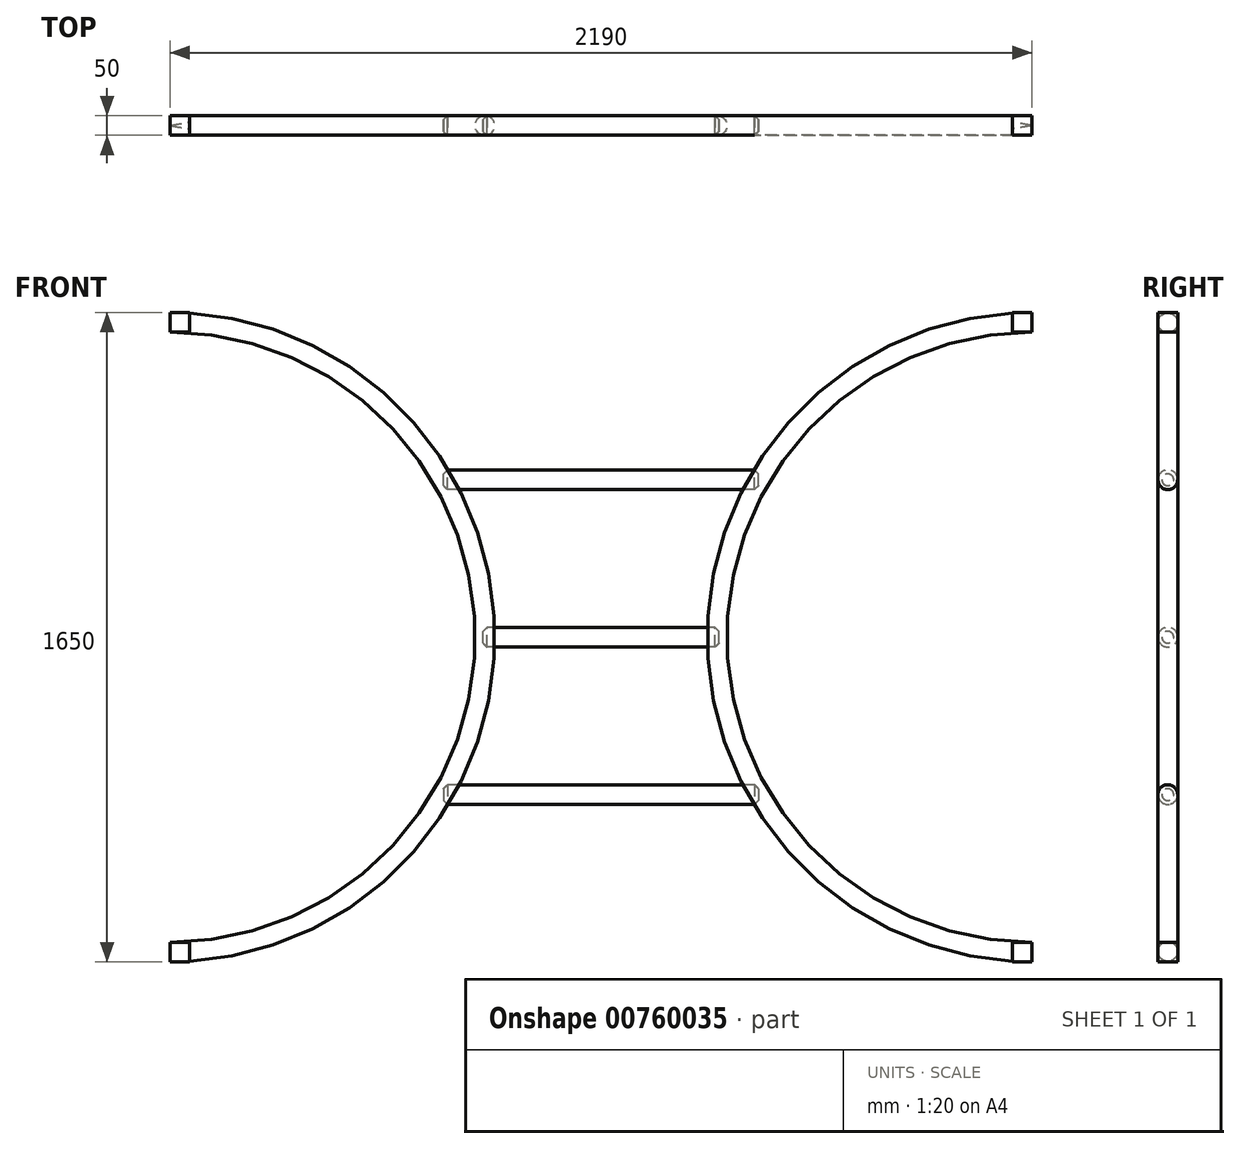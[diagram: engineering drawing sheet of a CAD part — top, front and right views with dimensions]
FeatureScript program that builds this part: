
annotation { "Feature Type Name" : "Feature", "Feature Type Description" : "" }
export const myFeature = defineFeature(function(context is Context, id is Id, definition is map)
    precondition{}
    {
        {
            var Q0;
            Q0=qCreatedBy(makeId("Front.planeOp"),FACE);
            var sketch = newSketch(context, id + "F0", { "sketchPlane" : qUnion([Q0])});
            skArc(sketch, "E0", {"start": v(0, 800) * mm, "mid": v(-800, 0) * mm, "end": v(0, -800) * mm});
            skSolve(sketch);
        }
        {
            var Q0;
            Q0=qCreatedBy(makeId("Right.planeOp"),FACE);
            var sketch = newSketch(context, id + "F1", { "sketchPlane" : qUnion([Q0])});
            skCircle(sketch, "E1", {"center": v(0, 800) * mm, "radius": 25 * mm});
            skSolve(sketch);
        }
        {
            var Q0;
            Q0=makeQuery(id+"F1.imprint","IMPRINT",FACE,{"disambiguationData":[TD([[makeQuery(id+"F1.imprint","IMPRINT",EDGE,{"derivedFrom":sQuery(id+"F1.wireOp",EDGE,"E1")}),1.0]])]});
            var Q1;
            Q1=sQuery(id+"F1.wireOp",EDGE,"E1");
            var Q2;
            Q2=sQuery(id+"F0.wireOp",EDGE,"E0");
            sweep(context, id + "F2", {"profiles" : qUnion([Q0]), "surfaceOperationType" : NewSurfaceOperationType.ADD, "surfaceProfiles" : qUnion([Q1]), "path" : qUnion([Q2])});
        }
        {
            var Q0;
            Q0=makeQuery(id+"F1.imprint","IMPRINT",FACE,{"disambiguationData":[TD([[makeQuery(id+"F1.imprint","IMPRINT",EDGE,{"derivedFrom":sQuery(id+"F1.wireOp",EDGE,"E1")}),1.0]])]});
            var sketch = newSketch(context, id + "F3", { "sketchPlane" : qUnion([Q0])});
            skLineSegment(sketch, "E2.bottom", {"start": v(-25, 825) * mm, "end": v(25, 825) * mm});
            skLineSegment(sketch, "E2.top", {"start": v(-25, 775) * mm, "end": v(25, 775) * mm});
            skLineSegment(sketch, "E2.left", {"start": v(-25, 825) * mm, "end": v(-25, 775) * mm});
            skLineSegment(sketch, "E2.right", {"start": v(25, 825) * mm, "end": v(25, 775) * mm});
            skSolve(sketch);
        }
        {
            var Q0;
            {var subQ0=sQuery(id+"F3.wireOp",EDGE,"E2.right");var subQ1=sQuery(id+"F3.wireOp",EDGE,"E2.bottom");var subQ2=makeQuery(id+"F3.imprint","INTERSECT",VERTEX,{"derivedFrom":[subQ1,subQ0]});Q0=makeQuery(id+"F3.imprint","IMPRINT",FACE,{"disambiguationData":[TD([[makeQuery(id+"F3.imprint","IMPRINT",EDGE,{"disambiguationData":[TD([[subQ2,1.0]])],"derivedFrom":subQ1}),-1.0]])]});}
            var Q1;
            {var subQ0=sQuery(id+"F3.wireOp",EDGE,"E2.left");var subQ1=sQuery(id+"F3.wireOp",EDGE,"E2.bottom");var subQ2=makeQuery(id+"F3.imprint","INTERSECT",VERTEX,{"derivedFrom":[subQ1,subQ0]});Q1=makeQuery(id+"F3.imprint","IMPRINT",FACE,{"disambiguationData":[TD([[makeQuery(id+"F3.imprint","IMPRINT",EDGE,{"disambiguationData":[TD([[subQ2,-1.0]])],"derivedFrom":subQ1}),-1.0]])]});}
            var Q2;
            {var subQ0=sQuery(id+"F3.wireOp",EDGE,"E2.left");var subQ1=sQuery(id+"F3.wireOp",EDGE,"E2.top");var subQ2=makeQuery(id+"F3.imprint","INTERSECT",VERTEX,{"derivedFrom":[subQ1,subQ0]});Q2=makeQuery(id+"F3.imprint","IMPRINT",FACE,{"disambiguationData":[TD([[makeQuery(id+"F3.imprint","IMPRINT",EDGE,{"disambiguationData":[TD([[subQ2,-1.0]])],"derivedFrom":subQ1}),1.0]])]});}
            var Q3;
            {var subQ0=sQuery(id+"F3.wireOp",EDGE,"E2.right");var subQ1=sQuery(id+"F3.wireOp",EDGE,"E2.top");var subQ2=makeQuery(id+"F3.imprint","INTERSECT",VERTEX,{"derivedFrom":[subQ1,subQ0]});Q3=makeQuery(id+"F3.imprint","IMPRINT",FACE,{"disambiguationData":[TD([[makeQuery(id+"F3.imprint","IMPRINT",EDGE,{"disambiguationData":[TD([[subQ2,1.0]])],"derivedFrom":subQ1}),1.0]])]});}
            var Q4;
            Q4=makeQuery(id+"F1.imprint","IMPRINT",FACE,{"disambiguationData":[TD([[makeQuery(id+"F1.imprint","IMPRINT",EDGE,{"derivedFrom":sQuery(id+"F1.wireOp",EDGE,"E1")}),1.0]])]});
            extrude(context, id + "F4", {"entities" : qUnion([Q0, Q1, Q2, Q3, Q4]), "operationType" : NewBodyOperationType.ADD, "oppositeDirection" : true, "depth" : 50 * mm, "offsetDistance" : 25 * mm});
        }
        {
            var Q0;
            Q0=makeQuery(id+"F2.opSweep","CAP_FACE",FACE,{"disambiguationData":[OSD([sQuery(id+"F0.wireOp",VERTEX,"E0.end"),sQuery(id+"F1.wireOp",EDGE,"E1")])],"isStart":false});
            var sketch = newSketch(context, id + "F5", { "sketchPlane" : qUnion([Q0])});
            skLineSegment(sketch, "E3.bottom", {"start": v(-25, -775) * mm, "end": v(25, -775) * mm});
            skLineSegment(sketch, "E3.top", {"start": v(-25, -825) * mm, "end": v(25, -825) * mm});
            skLineSegment(sketch, "E3.left", {"start": v(-25, -775) * mm, "end": v(-25, -825) * mm});
            skLineSegment(sketch, "E3.right", {"start": v(25, -775) * mm, "end": v(25, -825) * mm});
            skSolve(sketch);
        }
        {
            var Q0;
            {var subQ0=sQuery(id+"F5.wireOp",EDGE,"E3.left");var subQ1=sQuery(id+"F5.wireOp",EDGE,"E3.bottom");var subQ2=makeQuery(id+"F5.imprint","INTERSECT",VERTEX,{"derivedFrom":[subQ1,subQ0]});Q0=makeQuery(id+"F5.imprint","IMPRINT",FACE,{"disambiguationData":[TD([[makeQuery(id+"F5.imprint","IMPRINT",EDGE,{"disambiguationData":[TD([[subQ2,-1.0]])],"derivedFrom":subQ1}),-1.0]])]});}
            var Q1;
            {var subQ0=sQuery(id+"F5.wireOp",EDGE,"E3.right");var subQ1=sQuery(id+"F5.wireOp",EDGE,"E3.bottom");var subQ2=makeQuery(id+"F5.imprint","INTERSECT",VERTEX,{"derivedFrom":[subQ1,subQ0]});Q1=makeQuery(id+"F5.imprint","IMPRINT",FACE,{"disambiguationData":[TD([[makeQuery(id+"F5.imprint","IMPRINT",EDGE,{"disambiguationData":[TD([[subQ2,1.0]])],"derivedFrom":subQ1}),-1.0]])]});}
            var Q2;
            {var subQ0=sQuery(id+"F5.wireOp",EDGE,"E3.right");var subQ1=sQuery(id+"F5.wireOp",EDGE,"E3.top");var subQ2=makeQuery(id+"F5.imprint","INTERSECT",VERTEX,{"derivedFrom":[subQ1,subQ0]});Q2=makeQuery(id+"F5.imprint","IMPRINT",FACE,{"disambiguationData":[TD([[makeQuery(id+"F5.imprint","IMPRINT",EDGE,{"disambiguationData":[TD([[subQ2,1.0]])],"derivedFrom":subQ1}),1.0]])]});}
            var Q3;
            {var subQ0=sQuery(id+"F5.wireOp",EDGE,"E3.left");var subQ1=sQuery(id+"F5.wireOp",EDGE,"E3.top");var subQ2=makeQuery(id+"F5.imprint","INTERSECT",VERTEX,{"derivedFrom":[subQ1,subQ0]});Q3=makeQuery(id+"F5.imprint","IMPRINT",FACE,{"disambiguationData":[TD([[makeQuery(id+"F5.imprint","IMPRINT",EDGE,{"disambiguationData":[TD([[subQ2,-1.0]])],"derivedFrom":subQ1}),1.0]])]});}
            var Q4;
            {var subQ0=makeQuery(id+"F2.opSweep","CAP_EDGE",EDGE,{"disambiguationData":[OSD([sQuery(id+"F0.wireOp",VERTEX,"E0.end"),sQuery(id+"F1.wireOp",EDGE,"E1")])],"isStart":false});var subQ1=makeQuery(id+"F5.imprint","INTERSECT",VERTEX,{"derivedFrom":[subQ0,sQuery(id+"F5.wireOp",EDGE,"E3.bottom")]});Q4=makeQuery(id+"F5.imprint","IMPRINT",FACE,{"disambiguationData":[TD([[makeQuery(id+"F5.imprint","IMPRINT",EDGE,{"disambiguationData":[TD([[subQ1,-1.0]])],"derivedFrom":subQ0}),1.0]])]});}
            extrude(context, id + "F6", {"entities" : qUnion([Q0, Q1, Q2, Q3, Q4]), "operationType" : NewBodyOperationType.ADD, "oppositeDirection" : true, "depth" : 50 * mm, "offsetDistance" : 25 * mm});
        }
        {
            var Q0;
            Q0=qCreatedBy(makeId("Right.planeOp"),FACE);
            cPlane(context, id + "F7", {"entities" : qUnion([Q0]), "cplaneType" : CPlaneType.OFFSET, "offset" : (2190 / 2) * mm, "oppositeDirection" : true, "width" : 150 * mm, "height" : 150 * mm});
        }
        {
            var Q0;
            Q0=makeQuery(id+"F2.opSweep","SWEPT_BODY",BODY,{"disambiguationData":[OSD([sQuery(id+"F0.wireOp",EDGE,"E0"),sQuery(id+"F1.wireOp",EDGE,"E1")])]});
            var Q1;
            Q1=qCreatedBy(id+"F7.planeOp",FACE);
            mirror(context, id + "F8", {"entities" : qUnion([Q0]), "mirrorPlane" : qUnion([Q1])});
        }
        {
            var Q0;
            Q0=qCreatedBy(id+"F7.planeOp",FACE);
            var sketch = newSketch(context, id + "F9", { "sketchPlane" : qUnion([Q0])});
            skCircle(sketch, "E4", {"center": v(0, 0) * mm, "radius": 25 * mm});
            skCircle(sketch, "E5", {"center": v(0, 400) * mm, "radius": 25 * mm});
            skSolve(sketch);
        }
        {
            var Q0;
            Q0=makeQuery(id+"F9.imprint","IMPRINT",FACE,{"disambiguationData":[TD([[makeQuery(id+"F9.imprint","IMPRINT",EDGE,{"derivedFrom":sQuery(id+"F9.wireOp",EDGE,"E4")}),1.0]])]});
            extrude(context, id + "F10", {"entities" : qUnion([Q0]), "depth" : 600 * mm, "offsetDistance" : 25 * mm, "symmetric" : true});
        }
        {
            var Q0;
            Q0=makeQuery(id+"F10.opExtrude","CAP_EDGE",EDGE,{"disambiguationData":[OSD([sQuery(id+"F9.wireOp",EDGE,"E4")])],"isStart":true});
            var Q1;
            Q1=makeQuery(id+"F10.opExtrude","CAP_EDGE",EDGE,{"disambiguationData":[OSD([sQuery(id+"F9.wireOp",EDGE,"E4")])],"isStart":false});
            chamfer(context, id + "F11", {"entities" : qUnion([Q0, Q1]), "width" : 10 * mm, "tangentPropagation" : true});
        }
        {
            var Q0;
            Q0=makeQuery(id+"F9.imprint","IMPRINT",FACE,{"disambiguationData":[TD([[makeQuery(id+"F9.imprint","IMPRINT",EDGE,{"derivedFrom":sQuery(id+"F9.wireOp",EDGE,"E5")}),1.0]])]});
            extrude(context, id + "F12", {"entities" : qUnion([Q0]), "depth" : 800 * mm, "offsetDistance" : 25 * mm, "symmetric" : true});
        }
        {
            var Q0;
            Q0=makeQuery(id+"F12.opExtrude","CAP_EDGE",EDGE,{"disambiguationData":[OSD([sQuery(id+"F9.wireOp",EDGE,"E5")])],"isStart":true});
            var Q1;
            Q1=makeQuery(id+"F12.opExtrude","CAP_EDGE",EDGE,{"disambiguationData":[OSD([sQuery(id+"F9.wireOp",EDGE,"E5")])],"isStart":false});
            chamfer(context, id + "F13", {"entities" : qUnion([Q0, Q1]), "width" : 10 * mm, "tangentPropagation" : true});
        }
        {
            var Q0;
            Q0=makeQuery(id+"F12.opExtrude","SWEPT_BODY",BODY,{"disambiguationData":[OSD([sQuery(id+"F9.wireOp",EDGE,"E5")])]});
            var Q1;
            Q1=qCreatedBy(makeId("Top.planeOp"),FACE);
            mirror(context, id + "F14", {"entities" : qUnion([Q0]), "mirrorPlane" : qUnion([Q1])});
        }
    });
